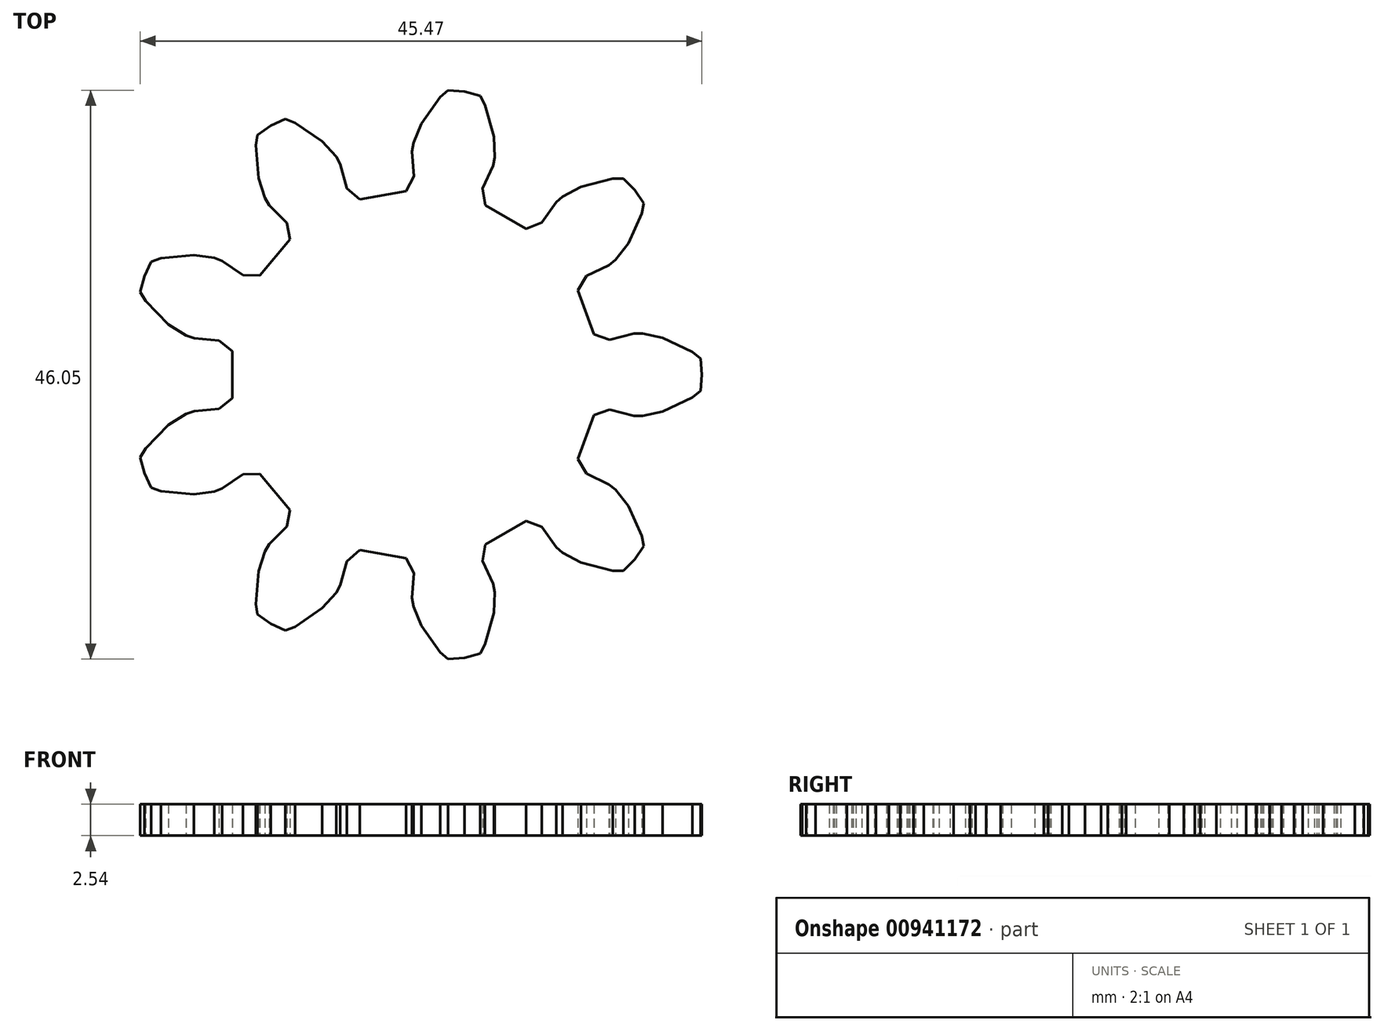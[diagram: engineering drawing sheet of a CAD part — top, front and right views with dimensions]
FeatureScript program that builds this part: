
annotation { "Feature Type Name" : "Feature", "Feature Type Description" : "" }
export const myFeature = defineFeature(function(context is Context, id is Id, definition is map)
    precondition{}
    {
        {
            var Q0;
            Q0=qCreatedBy(makeId("Top.planeOp"),FACE);
            var sketch = newSketch(context, id + "F0", { "sketchPlane" : qUnion([Q0])});
            skLineSegment(sketch, "E0", {"start": v(16.4, -15.98) * mm, "end": v(17.32, -15.05) * mm});
            skLineSegment(sketch, "E1", {"start": v(17.32, -15.05) * mm, "end": v(18.07, -13.98) * mm});
            skLineSegment(sketch, "E2", {"start": v(18.07, -13.98) * mm, "end": v(17.9, -13.15) * mm});
            skLineSegment(sketch, "E3", {"start": v(17.9, -13.15) * mm, "end": v(16.81, -10.73) * mm});
            skLineSegment(sketch, "E4", {"start": v(16.81, -10.73) * mm, "end": v(15.78, -9.4) * mm});
            skLineSegment(sketch, "E5", {"start": v(15.78, -9.4) * mm, "end": v(15.24, -8.97) * mm});
            skLineSegment(sketch, "E6", {"start": v(15.24, -8.97) * mm, "end": v(13.42, -8.1) * mm});
            skLineSegment(sketch, "E7", {"start": v(13.42, -8.1) * mm, "end": v(12.71, -6.93) * mm});
            skLineSegment(sketch, "E8", {"start": v(12.71, -6.93) * mm, "end": v(14.01, -3.36) * mm});
            skLineSegment(sketch, "E9", {"start": v(14.01, -3.36) * mm, "end": v(15.3, -2.91) * mm});
            skLineSegment(sketch, "E10", {"start": v(15.3, -2.91) * mm, "end": v(17.26, -3.42) * mm});
            skLineSegment(sketch, "E11", {"start": v(17.26, -3.42) * mm, "end": v(17.96, -3.43) * mm});
            skLineSegment(sketch, "E12", {"start": v(17.96, -3.43) * mm, "end": v(19.6, -3.08) * mm});
            skLineSegment(sketch, "E13", {"start": v(19.6, -3.08) * mm, "end": v(22, -1.93) * mm});
            skLineSegment(sketch, "E14", {"start": v(22, -1.93) * mm, "end": v(22.65, -1.4) * mm});
            skLineSegment(sketch, "E15", {"start": v(22.65, -1.4) * mm, "end": v(22.76, -0.1) * mm});
            skLineSegment(sketch, "E16", {"start": v(22.76, -0.1) * mm, "end": v(22.65, 1.21) * mm});
            skLineSegment(sketch, "E17", {"start": v(22.65, 1.21) * mm, "end": v(22, 1.74) * mm});
            skLineSegment(sketch, "E18", {"start": v(22, 1.74) * mm, "end": v(19.6, 2.89) * mm});
            skLineSegment(sketch, "E19", {"start": v(19.6, 2.89) * mm, "end": v(17.96, 3.24) * mm});
            skLineSegment(sketch, "E20", {"start": v(17.96, 3.24) * mm, "end": v(17.26, 3.23) * mm});
            skLineSegment(sketch, "E21", {"start": v(17.26, 3.23) * mm, "end": v(15.3, 2.72) * mm});
            skLineSegment(sketch, "E22", {"start": v(15.3, 2.72) * mm, "end": v(14.01, 3.16) * mm});
            skLineSegment(sketch, "E23", {"start": v(14.01, 3.16) * mm, "end": v(12.71, 6.74) * mm});
            skLineSegment(sketch, "E24", {"start": v(12.71, 6.74) * mm, "end": v(13.42, 7.9) * mm});
            skLineSegment(sketch, "E25", {"start": v(13.42, 7.9) * mm, "end": v(15.24, 8.78) * mm});
            skLineSegment(sketch, "E26", {"start": v(15.24, 8.78) * mm, "end": v(15.78, 9.21) * mm});
            skLineSegment(sketch, "E27", {"start": v(15.78, 9.21) * mm, "end": v(16.81, 10.54) * mm});
            skLineSegment(sketch, "E28", {"start": v(16.81, 10.54) * mm, "end": v(17.9, 12.96) * mm});
            skLineSegment(sketch, "E29", {"start": v(17.9, 12.96) * mm, "end": v(18.07, 13.78) * mm});
            skLineSegment(sketch, "E30", {"start": v(18.07, 13.78) * mm, "end": v(17.32, 14.86) * mm});
            skLineSegment(sketch, "E31", {"start": v(17.32, 14.86) * mm, "end": v(16.4, 15.79) * mm});
            skLineSegment(sketch, "E32", {"start": v(16.4, 15.79) * mm, "end": v(15.55, 15.77) * mm});
            skLineSegment(sketch, "E33", {"start": v(15.55, 15.77) * mm, "end": v(12.98, 15.1) * mm});
            skLineSegment(sketch, "E34", {"start": v(12.98, 15.1) * mm, "end": v(11.5, 14.33) * mm});
            skLineSegment(sketch, "E35", {"start": v(11.5, 14.33) * mm, "end": v(10.97, 13.87) * mm});
            skLineSegment(sketch, "E36", {"start": v(10.97, 13.87) * mm, "end": v(9.8, 12.22) * mm});
            skLineSegment(sketch, "E37", {"start": v(9.8, 12.22) * mm, "end": v(8.52, 11.73) * mm});
            skLineSegment(sketch, "E38", {"start": v(8.52, 11.73) * mm, "end": v(5.23, 13.63) * mm});
            skLineSegment(sketch, "E39", {"start": v(5.23, 13.63) * mm, "end": v(5.02, 14.98) * mm});
            skLineSegment(sketch, "E40", {"start": v(5.02, 14.98) * mm, "end": v(5.85, 16.82) * mm});
            skLineSegment(sketch, "E41", {"start": v(5.85, 16.82) * mm, "end": v(5.99, 17.5) * mm});
            skLineSegment(sketch, "E42", {"start": v(5.99, 17.5) * mm, "end": v(5.92, 19.18) * mm});
            skLineSegment(sketch, "E43", {"start": v(5.92, 19.18) * mm, "end": v(5.21, 21.74) * mm});
            skLineSegment(sketch, "E44", {"start": v(5.21, 21.74) * mm, "end": v(4.8, 22.48) * mm});
            skLineSegment(sketch, "E45", {"start": v(4.8, 22.48) * mm, "end": v(3.54, 22.82) * mm});
            skLineSegment(sketch, "E46", {"start": v(3.54, 22.82) * mm, "end": v(2.23, 22.93) * mm});
            skLineSegment(sketch, "E47", {"start": v(2.23, 22.93) * mm, "end": v(1.6, 22.38) * mm});
            skLineSegment(sketch, "E48", {"start": v(1.6, 22.38) * mm, "end": v(0.05, 20.22) * mm});
            skLineSegment(sketch, "E49", {"start": v(0.05, 20.22) * mm, "end": v(-0.59, 18.67) * mm});
            skLineSegment(sketch, "E50", {"start": v(-0.59, 18.67) * mm, "end": v(-0.7, 17.98) * mm});
            skLineSegment(sketch, "E51", {"start": v(-0.7, 17.98) * mm, "end": v(-0.54, 15.96) * mm});
            skLineSegment(sketch, "E52", {"start": v(-0.54, 15.96) * mm, "end": v(-1.2, 14.77) * mm});
            skLineSegment(sketch, "E53", {"start": v(-1.2, 14.77) * mm, "end": v(-4.94, 14.1) * mm});
            skLineSegment(sketch, "E54", {"start": v(-4.94, 14.1) * mm, "end": v(-5.97, 15) * mm});
            skLineSegment(sketch, "E55", {"start": v(-5.97, 15) * mm, "end": v(-6.5, 16.95) * mm});
            skLineSegment(sketch, "E56", {"start": v(-6.5, 16.95) * mm, "end": v(-6.85, 17.56) * mm});
            skLineSegment(sketch, "E57", {"start": v(-6.85, 17.56) * mm, "end": v(-7.97, 18.8) * mm});
            skLineSegment(sketch, "E58", {"start": v(-7.97, 18.8) * mm, "end": v(-10.16, 20.3) * mm});
            skLineSegment(sketch, "E59", {"start": v(-10.16, 20.3) * mm, "end": v(-10.95, 20.6) * mm});
            skLineSegment(sketch, "E60", {"start": v(-10.95, 20.6) * mm, "end": v(-12.14, 20.05) * mm});
            skLineSegment(sketch, "E61", {"start": v(-12.14, 20.05) * mm, "end": v(-13.21, 19.3) * mm});
            skLineSegment(sketch, "E62", {"start": v(-13.21, 19.3) * mm, "end": v(-13.34, 18.47) * mm});
            skLineSegment(sketch, "E63", {"start": v(-13.34, 18.47) * mm, "end": v(-13.14, 15.82) * mm});
            skLineSegment(sketch, "E64", {"start": v(-13.14, 15.82) * mm, "end": v(-12.63, 14.22) * mm});
            skLineSegment(sketch, "E65", {"start": v(-12.63, 14.22) * mm, "end": v(-12.27, 13.63) * mm});
            skLineSegment(sketch, "E66", {"start": v(-12.27, 13.63) * mm, "end": v(-10.85, 12.18) * mm});
            skLineSegment(sketch, "E67", {"start": v(-10.85, 12.18) * mm, "end": v(-10.59, 10.85) * mm});
            skLineSegment(sketch, "E68", {"start": v(-10.59, 10.85) * mm, "end": v(-13.03, 7.93) * mm});
            skLineSegment(sketch, "E69", {"start": v(-13.03, 7.93) * mm, "end": v(-14.4, 7.96) * mm});
            skLineSegment(sketch, "E70", {"start": v(-14.4, 7.96) * mm, "end": v(-16.06, 9.1) * mm});
            skLineSegment(sketch, "E71", {"start": v(-16.06, 9.1) * mm, "end": v(-16.71, 9.36) * mm});
            skLineSegment(sketch, "E72", {"start": v(-16.71, 9.36) * mm, "end": v(-18.37, 9.58) * mm});
            skLineSegment(sketch, "E73", {"start": v(-18.37, 9.58) * mm, "end": v(-21.01, 9.33) * mm});
            skLineSegment(sketch, "E74", {"start": v(-21.01, 9.33) * mm, "end": v(-21.81, 9.05) * mm});
            skLineSegment(sketch, "E75", {"start": v(-21.81, 9.05) * mm, "end": v(-22.37, 7.86) * mm});
            skLineSegment(sketch, "E76", {"start": v(-22.37, 7.86) * mm, "end": v(-22.7, 6.6) * mm});
            skLineSegment(sketch, "E77", {"start": v(-22.7, 6.6) * mm, "end": v(-22.27, 5.87) * mm});
            skLineSegment(sketch, "E78", {"start": v(-22.27, 5.87) * mm, "end": v(-20.41, 3.98) * mm});
            skLineSegment(sketch, "E79", {"start": v(-20.41, 3.98) * mm, "end": v(-19, 3.08) * mm});
            skLineSegment(sketch, "E80", {"start": v(-19, 3.08) * mm, "end": v(-18.34, 2.86) * mm});
            skLineSegment(sketch, "E81", {"start": v(-18.34, 2.86) * mm, "end": v(-16.32, 2.66) * mm});
            skLineSegment(sketch, "E82", {"start": v(-16.32, 2.66) * mm, "end": v(-15.26, 1.8) * mm});
            skLineSegment(sketch, "E83", {"start": v(-15.26, 1.8) * mm, "end": v(-15.26, -2) * mm});
            skLineSegment(sketch, "E84", {"start": v(-15.26, -2) * mm, "end": v(-16.32, -2.85) * mm});
            skLineSegment(sketch, "E85", {"start": v(-16.32, -2.85) * mm, "end": v(-18.34, -3.05) * mm});
            skLineSegment(sketch, "E86", {"start": v(-18.34, -3.05) * mm, "end": v(-19, -3.27) * mm});
            skLineSegment(sketch, "E87", {"start": v(-19, -3.27) * mm, "end": v(-20.41, -4.17) * mm});
            skLineSegment(sketch, "E88", {"start": v(-20.41, -4.17) * mm, "end": v(-22.27, -6.06) * mm});
            skLineSegment(sketch, "E89", {"start": v(-22.27, -6.06) * mm, "end": v(-22.7, -6.78) * mm});
            skLineSegment(sketch, "E90", {"start": v(-22.7, -6.78) * mm, "end": v(-22.37, -8.05) * mm});
            skLineSegment(sketch, "E91", {"start": v(-22.37, -8.05) * mm, "end": v(-21.81, -9.24) * mm});
            skLineSegment(sketch, "E92", {"start": v(-21.81, -9.24) * mm, "end": v(-21.01, -9.52) * mm});
            skLineSegment(sketch, "E93", {"start": v(-21.01, -9.52) * mm, "end": v(-18.37, -9.77) * mm});
            skLineSegment(sketch, "E94", {"start": v(-18.37, -9.77) * mm, "end": v(-16.71, -9.55) * mm});
            skLineSegment(sketch, "E95", {"start": v(-16.71, -9.55) * mm, "end": v(-16.06, -9.3) * mm});
            skLineSegment(sketch, "E96", {"start": v(-16.06, -9.3) * mm, "end": v(-14.4, -8.15) * mm});
            skLineSegment(sketch, "E97", {"start": v(-14.4, -8.15) * mm, "end": v(-13.03, -8.12) * mm});
            skLineSegment(sketch, "E98", {"start": v(-13.03, -8.12) * mm, "end": v(-10.59, -11.04) * mm});
            skLineSegment(sketch, "E99", {"start": v(-10.59, -11.04) * mm, "end": v(-10.85, -12.38) * mm});
            skLineSegment(sketch, "E100", {"start": v(-10.85, -12.38) * mm, "end": v(-12.27, -13.82) * mm});
            skLineSegment(sketch, "E101", {"start": v(-12.27, -13.82) * mm, "end": v(-12.63, -14.42) * mm});
            skLineSegment(sketch, "E102", {"start": v(-12.63, -14.42) * mm, "end": v(-13.14, -16.01) * mm});
            skLineSegment(sketch, "E103", {"start": v(-13.14, -16.01) * mm, "end": v(-13.34, -18.66) * mm});
            skLineSegment(sketch, "E104", {"start": v(-13.34, -18.66) * mm, "end": v(-13.21, -19.5) * mm});
            skLineSegment(sketch, "E105", {"start": v(-13.21, -19.5) * mm, "end": v(-12.14, -20.25) * mm});
            skLineSegment(sketch, "E106", {"start": v(-12.14, -20.25) * mm, "end": v(-10.95, -20.8) * mm});
            skLineSegment(sketch, "E107", {"start": v(-10.95, -20.8) * mm, "end": v(-10.16, -20.5) * mm});
            skLineSegment(sketch, "E108", {"start": v(-10.16, -20.5) * mm, "end": v(-7.97, -19) * mm});
            skLineSegment(sketch, "E109", {"start": v(-7.97, -19) * mm, "end": v(-6.85, -17.75) * mm});
            skLineSegment(sketch, "E110", {"start": v(-6.85, -17.75) * mm, "end": v(-6.5, -17.14) * mm});
            skLineSegment(sketch, "E111", {"start": v(-6.5, -17.14) * mm, "end": v(-5.97, -15.2) * mm});
            skLineSegment(sketch, "E112", {"start": v(-5.97, -15.2) * mm, "end": v(-4.94, -14.3) * mm});
            skLineSegment(sketch, "E113", {"start": v(-4.94, -14.3) * mm, "end": v(-1.2, -14.96) * mm});
            skLineSegment(sketch, "E114", {"start": v(-1.2, -14.96) * mm, "end": v(-0.54, -16.15) * mm});
            skLineSegment(sketch, "E115", {"start": v(-0.54, -16.15) * mm, "end": v(-0.7, -18.17) * mm});
            skLineSegment(sketch, "E116", {"start": v(-0.7, -18.17) * mm, "end": v(-0.59, -18.86) * mm});
            skLineSegment(sketch, "E117", {"start": v(-0.59, -18.86) * mm, "end": v(0.05, -20.4) * mm});
            skLineSegment(sketch, "E118", {"start": v(0.05, -20.4) * mm, "end": v(1.6, -22.57) * mm});
            skLineSegment(sketch, "E119", {"start": v(1.6, -22.57) * mm, "end": v(2.23, -23.12) * mm});
            skLineSegment(sketch, "E120", {"start": v(2.23, -23.12) * mm, "end": v(3.54, -23) * mm});
            skLineSegment(sketch, "E121", {"start": v(3.54, -23) * mm, "end": v(4.8, -22.67) * mm});
            skLineSegment(sketch, "E122", {"start": v(4.8, -22.67) * mm, "end": v(5.21, -21.93) * mm});
            skLineSegment(sketch, "E123", {"start": v(5.21, -21.93) * mm, "end": v(5.92, -19.37) * mm});
            skLineSegment(sketch, "E124", {"start": v(5.92, -19.37) * mm, "end": v(5.99, -17.7) * mm});
            skLineSegment(sketch, "E125", {"start": v(5.99, -17.7) * mm, "end": v(5.85, -17.01) * mm});
            skLineSegment(sketch, "E126", {"start": v(5.85, -17.01) * mm, "end": v(5.02, -15.17) * mm});
            skLineSegment(sketch, "E127", {"start": v(5.02, -15.17) * mm, "end": v(5.23, -13.83) * mm});
            skLineSegment(sketch, "E128", {"start": v(5.23, -13.83) * mm, "end": v(8.52, -11.92) * mm});
            skLineSegment(sketch, "E129", {"start": v(8.52, -11.92) * mm, "end": v(9.8, -12.42) * mm});
            skLineSegment(sketch, "E130", {"start": v(9.8, -12.42) * mm, "end": v(10.97, -14.06) * mm});
            skLineSegment(sketch, "E131", {"start": v(10.97, -14.06) * mm, "end": v(11.5, -14.52) * mm});
            skLineSegment(sketch, "E132", {"start": v(11.5, -14.52) * mm, "end": v(12.98, -15.3) * mm});
            skLineSegment(sketch, "E133", {"start": v(12.98, -15.3) * mm, "end": v(15.55, -15.96) * mm});
            skLineSegment(sketch, "E134", {"start": v(15.55, -15.96) * mm, "end": v(16.4, -15.98) * mm});
            skSolve(sketch);
        }
        {
            var Q0;
            Q0=qSketchRegion(id+"F0",true);
            extrude(context, id + "F1", {"entities" : qUnion([Q0]), "depth" : 2.54 * mm, "offsetDistance" : 25.4 * mm});
        }
    });
